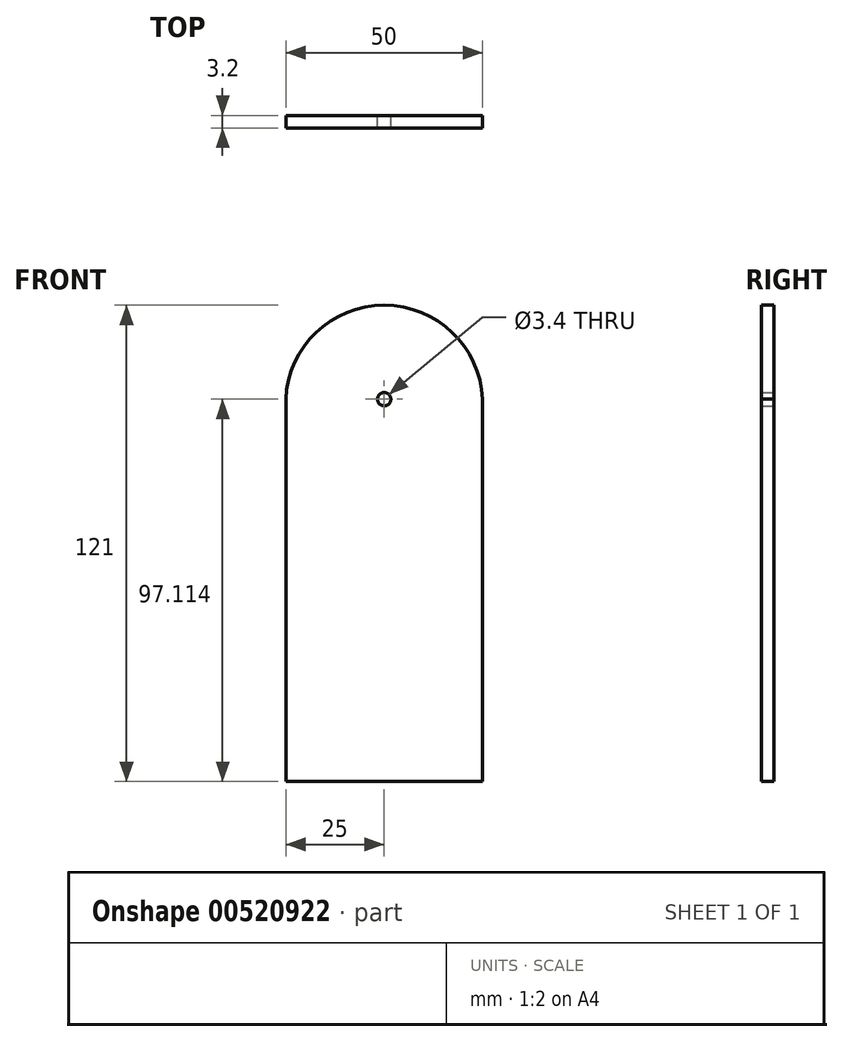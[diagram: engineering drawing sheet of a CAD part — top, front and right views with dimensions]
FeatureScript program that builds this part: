
annotation { "Feature Type Name" : "Feature", "Feature Type Description" : "" }
export const myFeature = defineFeature(function(context is Context, id is Id, definition is map)
    precondition{}
    {
        {
            var Q0;
            Q0=qCreatedBy(makeId("Front.planeOp"),FACE);
            var sketch = newSketch(context, id + "F0", { "sketchPlane" : qUnion([Q0])});
            skLineSegment(sketch, "E0.bottom", {"start": v(-24.7, 55.16) * mm, "end": v(25.3, 55.16) * mm, "construction": true});
            skLineSegment(sketch, "E0.top", {"start": v(-25, -65.84) * mm, "end": v(25, -65.84) * mm});
            skArc(sketch, "E1", {"start": v(25, 31.28) * mm, "mid": v(0, 55.16) * mm, "end": v(-25, 31.27) * mm});
            skLineSegment(sketch, "E2", {"start": v(-25, -65.84) * mm, "end": v(-25, 31.27) * mm});
            skLineSegment(sketch, "E3", {"start": v(25, -65.84) * mm, "end": v(25, 31.28) * mm});
            skCircle(sketch, "E4", {"center": v(0, 31.27) * mm, "radius": 1.7 * mm});
            skLineSegment(sketch, "E5.top", {"start": v(0, -65.84) * mm, "end": v(25, -65.84) * mm});
            skLineSegment(sketch, "E6", {"start": v(25, 31.28) * mm, "end": v(-25, 31.27) * mm, "construction": true});
            skSolve(sketch);
        }
        {
            var Q0;
            Q0=makeQuery(id+"F0.imprint","IMPRINT",FACE,{"disambiguationData":[TD([[makeQuery(id+"F0.imprint","IMPRINT",EDGE,{"derivedFrom":sQuery(id+"F0.wireOp",EDGE,"E1")}),1.0]])]});
            extrude(context, id + "F1", {"entities" : qUnion([Q0]), "depth" : 3.2 * mm, "offsetDistance" : 25 * mm});
        }
    });
